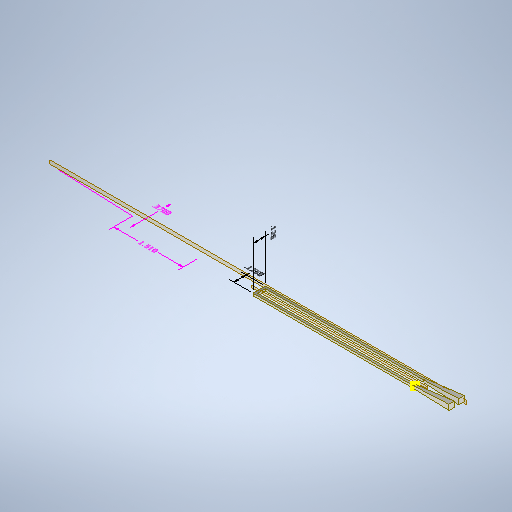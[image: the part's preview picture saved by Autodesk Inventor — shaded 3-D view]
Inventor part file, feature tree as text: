
AUTODESK INVENTOR PART (.ipt)
format: ipt  version: 2025.2 (Build 292293000, 293)  size: 307,712 bytes
history: native  units: in
note: dims shown in document units (in); Inventor stores cm internally (conversion verified against a paired STEP export)
features: other x6, plane x4, sketch x4, sweep x1, loft x1, mirror x1, projected_geometry x1
ambient origin geometry x8: Origin, YZ Plane, XZ Plane, XY Plane, X Axis, Y Axis, Z Axis, Center Point
bodies: Solid1 (feature_tree)
feature tree (18):
  other  "Annotations"
  sweep  "Sweep1"
  plane  "Work Plane1"
  plane  "Work Plane2"
  plane  "Work Plane4"
  sketch  "Sketch15"  dims[d86=-0.1175in]
  sketch  "Sketch16"  dims[d89=0.1in d90=0.0in d91=0.0in d92=0.0in d98=0.023in d99=0.023in d100=0.055in d102=0.055in d104=0.0in d109=0.0in d110=90.0deg d111=0.0in d112=90.0deg d116=-0.063in d113=0.0in d114=0.3937in d115=0.126in d117=0.0226in d118=0.3734in d119=0.126in d42=0.2341in d43=0.169in d44=0.37in d48=0.2141in d49=0.2512in d50=1.51in]
  loft  "Loft3"
  plane  "Work Plane5"
  mirror  "Mirror3"
  sketch  "Sketch1"  dims[d6=0.0in d7=0.0in d11=0.375in d19=-0.25in]
  sketch  "Sketch2"  dims[d69=1.625in d70=1.625in]
  projected_geometry  "Projected Loop1"
  other  "Edges4"
  other  "Linear Dimension 1"
  other  "Linear Dimension 3"
  other  "Linear Dimension 4"
  other  "Linear Dimension 5"
